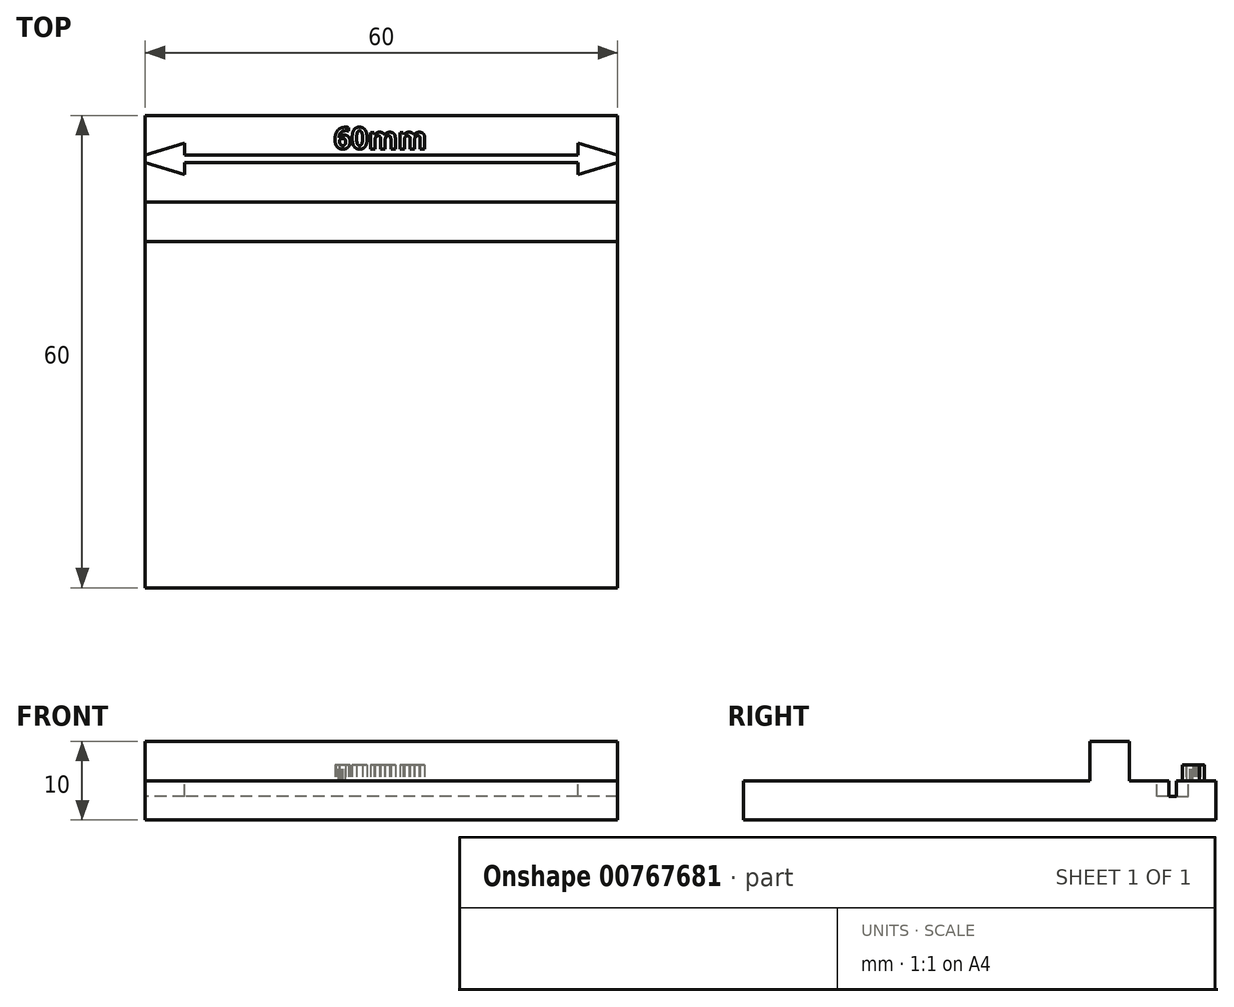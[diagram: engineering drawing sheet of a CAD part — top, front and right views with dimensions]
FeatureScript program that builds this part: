
annotation { "Feature Type Name" : "Feature", "Feature Type Description" : "" }
export const myFeature = defineFeature(function(context is Context, id is Id, definition is map)
    precondition{}
    {
        {
            var Q0;
            Q0=qCreatedBy(makeId("Top.planeOp"),FACE);
            var sketch = newSketch(context, id + "F0", { "sketchPlane" : qUnion([Q0])});
            skLineSegment(sketch, "E0.bottom", {"start": v(30, -30) * mm, "end": v(-30, -30) * mm});
            skLineSegment(sketch, "E0.top", {"start": v(30, 30) * mm, "end": v(-30, 30) * mm});
            skLineSegment(sketch, "E0.left", {"start": v(30, -30) * mm, "end": v(30, 30) * mm});
            skLineSegment(sketch, "E0.right", {"start": v(-30, -30) * mm, "end": v(-30, 30) * mm});
            skPoint(sketch, "E0.middle", {"position": v(0, 0) * mm});
            skSolve(sketch);
        }
        {
            var Q0;
            Q0 = qSketchRegion(id + "F0", true);
            extrude(context, id + "F1", {"entities" : qUnion([Q0]), "depth" : 5 * mm, "offsetDistance" : 25 * mm});
        }
        {
            var Q0;
            Q0=makeQuery(id+"F1.opExtrude","CAP_FACE",FACE,{"disambiguationData":[OSD([sQuery(id+"F0.wireOp",EDGE,"E0.bottom"),sQuery(id+"F0.wireOp",EDGE,"E0.top"),sQuery(id+"F0.wireOp",EDGE,"E0.left"),sQuery(id+"F0.wireOp",EDGE,"E0.right")])],"isStart":false});
            var sketch = newSketch(context, id + "F2", { "sketchPlane" : qUnion([Q0])});
            skLineSegment(sketch, "E1", {"start": v(0, 25) * mm, "end": v(25, 25) * mm});
            skLineSegment(sketch, "E2", {"start": v(0, 25) * mm, "end": v(-25, 25) * mm});
            skLineSegment(sketch, "E3.0", {"start": v(0, 24) * mm, "end": v(25, 24) * mm});
            skLineSegment(sketch, "E3.1", {"start": v(0, 24) * mm, "end": v(-25, 24) * mm});
            skLineSegment(sketch, "E4", {"start": v(-25, 25) * mm, "end": v(-25, 26.5) * mm});
            skLineSegment(sketch, "E5", {"start": v(-25, 24) * mm, "end": v(-25, 22.5) * mm});
            skLineSegment(sketch, "E6", {"start": v(-25, 26.5) * mm, "end": v(-30, 25) * mm});
            skLineSegment(sketch, "E7", {"start": v(-30, 24) * mm, "end": v(-25, 22.5) * mm});
            skLineSegment(sketch, "E8", {"start": v(-30, 25) * mm, "end": v(-30, 24) * mm});
            skLineSegment(sketch, "E9.MirrorCS", {"start": v(25, 26.5) * mm, "end": v(30, 25) * mm});
            skLineSegment(sketch, "E10.MirrorCS", {"start": v(30, 25) * mm, "end": v(30, 24) * mm});
            skLineSegment(sketch, "E11.MirrorCS", {"start": v(30, 24) * mm, "end": v(25, 22.5) * mm});
            skLineSegment(sketch, "E12.MirrorCS", {"start": v(25, 25) * mm, "end": v(25, 26.5) * mm});
            skLineSegment(sketch, "E13.MirrorCS", {"start": v(25, 24) * mm, "end": v(25, 22.5) * mm});
            skSolve(sketch);
        }
        {
            var Q0;
            Q0=makeQuery(id+"F2.imprint","IMPRINT",FACE,{"disambiguationData":[TD([[makeQuery(id+"F2.imprint","IMPRINT",EDGE,{"derivedFrom":sQuery(id+"F2.wireOp",EDGE,"E1")}),-1.0]])]});
            extrude(context, id + "F3", {"entities" : qUnion([Q0]), "operationType" : NewBodyOperationType.REMOVE, "oppositeDirection" : true, "depth" : 2 * mm, "offsetDistance" : 25 * mm});
        }
        {
            var Q0;
            Q0 = qSketchRegion(id + "F2", true);
            extrude(context, id + "F4", {"entities" : qUnion([Q0]), "operationType" : NewBodyOperationType.REMOVE, "oppositeDirection" : true, "depth" : 2 * mm, "offsetDistance" : 25 * mm});
        }
        {
            var Q0;
            {var subQ0=sQuery(id+"F0.wireOp",EDGE,"E0.right");var subQ1=sQuery(id+"F0.wireOp",EDGE,"E0.left");var subQ2=sQuery(id+"F0.wireOp",EDGE,"E0.top");Q0=makeQuery(id+"F3.boolean.opBoolean","SPLIT",FACE,{"disambiguationData":[TD([makeQuery(id+"F1.opExtrude","SWEPT_FACE",FACE,{"disambiguationData":[OSD([subQ2])]})])],"derivedFrom":makeQuery(id+"F1.opExtrude","CAP_FACE",FACE,{"disambiguationData":[OSD([sQuery(id+"F0.wireOp",EDGE,"E0.bottom"),subQ2,subQ1,subQ0])],"isStart":false})});}
            var sketch = newSketch(context, id + "F5", { "sketchPlane" : qUnion([Q0])});
            skText(sketch, "E14", { "text": "60mm\n", "fontName": "OpenSans-Bold.ttf"});
            const initialGuessF5  = {"E14": [-0.00603, 0.02576, 1, 0, 0.00274]};
            skSetInitialGuess(sketch, initialGuessF5);
            skSolve(sketch);
        }
        {
            var Q0;
            Q0 = qSketchRegion(id + "F5", true);
            extrude(context, id + "F6", {"entities" : qUnion([Q0]), "operationType" : NewBodyOperationType.ADD, "depth" : 2 * mm, "offsetDistance" : 25 * mm});
        }
        {
            var Q0;
            {var subQ0=sQuery(id+"F0.wireOp",EDGE,"E0.left");var subQ1=sQuery(id+"F0.wireOp",EDGE,"E0.right");var subQ2=sQuery(id+"F0.wireOp",EDGE,"E0.bottom");Q0=makeQuery(id+"F3.boolean.opBoolean","SPLIT",FACE,{"disambiguationData":[TD([makeQuery(id+"F1.opExtrude","SWEPT_FACE",FACE,{"disambiguationData":[OSD([subQ2])]})])],"derivedFrom":makeQuery(id+"F1.opExtrude","CAP_FACE",FACE,{"disambiguationData":[OSD([subQ2,sQuery(id+"F0.wireOp",EDGE,"E0.top"),subQ0,subQ1])],"isStart":false})});}
            var sketch = newSketch(context, id + "F7", { "sketchPlane" : qUnion([Q0])});
            skLineSegment(sketch, "E15", {"start": v(0, 0) * mm, "end": v(0, 14) * mm});
            skLineSegment(sketch, "E16", {"start": v(0, 14) * mm, "end": v(-30, 14) * mm});
            skLineSegment(sketch, "E17", {"start": v(-30, 14) * mm, "end": v(-30, 19) * mm});
            skLineSegment(sketch, "E18", {"start": v(-30, 19) * mm, "end": v(30, 19) * mm});
            skLineSegment(sketch, "E19", {"start": v(0, 14) * mm, "end": v(30, 14) * mm});
            skLineSegment(sketch, "E20", {"start": v(30, 19) * mm, "end": v(30, 14) * mm});
            skSolve(sketch);
        }
        {
            var Q0;
            Q0 = qSketchRegion(id + "F7", true);
            extrude(context, id + "F8", {"entities" : qUnion([Q0]), "operationType" : NewBodyOperationType.ADD, "depth" : 5 * mm, "offsetDistance" : 25 * mm});
        }
    });
